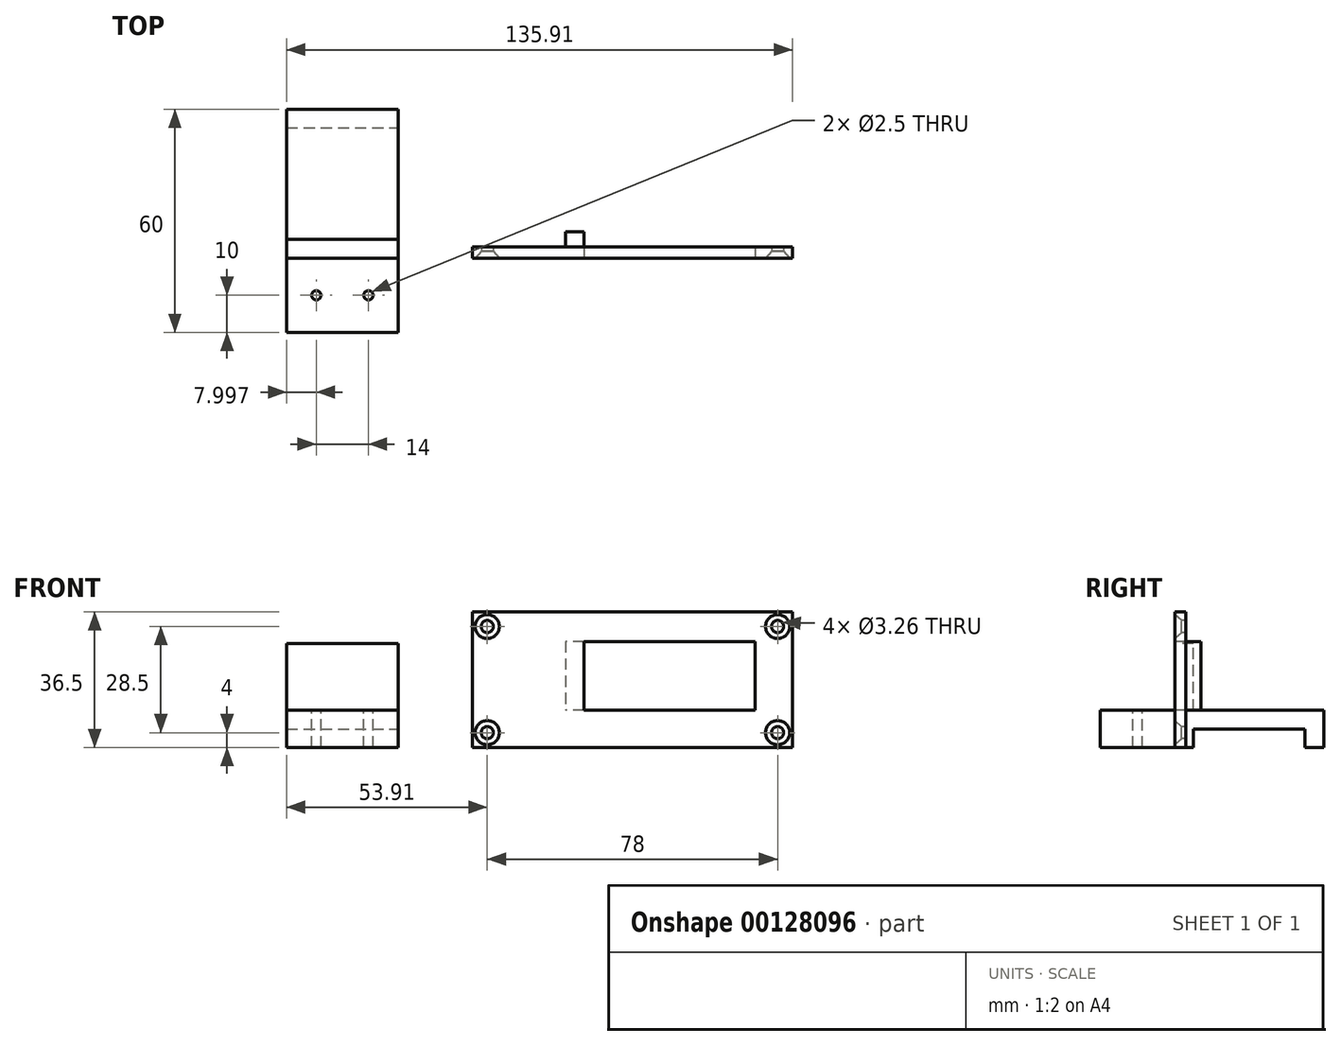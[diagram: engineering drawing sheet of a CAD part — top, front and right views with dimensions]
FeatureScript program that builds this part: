
annotation { "Feature Type Name" : "Feature", "Feature Type Description" : "" }
export const myFeature = defineFeature(function(context is Context, id is Id, definition is map)
    precondition{}
    {
        {
            var Q0;
            Q0=qCreatedBy(makeId("Front.planeOp"),FACE);
            var sketch = newSketch(context, id + "F0", { "sketchPlane" : qUnion([Q0])});
            skLineSegment(sketch, "E0.bottom", {"start": v(0, 18.5) * mm, "end": v(46, 18.5) * mm});
            skLineSegment(sketch, "E0.top", {"start": v(0, 0) * mm, "end": v(46, 0) * mm});
            skLineSegment(sketch, "E0.left", {"start": v(0, 18.5) * mm, "end": v(0, 0) * mm});
            skLineSegment(sketch, "E0.right", {"start": v(46, 18.5) * mm, "end": v(46, 0) * mm});
            skPoint(sketch, "E1.positionSnap0", {"position": v(0, 9.25) * mm});
            skLineSegment(sketch, "E2.bottom", {"start": v(-30, 26.5) * mm, "end": v(56, 26.5) * mm});
            skLineSegment(sketch, "E2.top", {"start": v(-30, -10) * mm, "end": v(56, -10) * mm});
            skLineSegment(sketch, "E2.left", {"start": v(-30, 26.5) * mm, "end": v(-30, -10) * mm});
            skLineSegment(sketch, "E2.right", {"start": v(56, 26.5) * mm, "end": v(56, -10) * mm});
            skPoint(sketch, "E3", {"position": v(52, 22.5) * mm});
            skPoint(sketch, "E4", {"position": v(-26, -6) * mm});
            skPoint(sketch, "E5", {"position": v(-26, 22.5) * mm});
            skPoint(sketch, "E6", {"position": v(52, -6) * mm});
            skLineSegment(sketch, "E7.bottom", {"start": v(0, 18.5) * mm, "end": v(-5, 18.5) * mm});
            skLineSegment(sketch, "E7.top", {"start": v(0, 0) * mm, "end": v(-5, 0) * mm});
            skLineSegment(sketch, "E7.right", {"start": v(-5, 18.5) * mm, "end": v(-5, 0) * mm});
            skSolve(sketch);
        }
        {
            var Q0;
            Q0=makeQuery(id+"F0.imprint","IMPRINT",FACE,{"disambiguationData":[TD([[makeQuery(id+"F0.imprint","IMPRINT",EDGE,{"derivedFrom":sQuery(id+"F0.wireOp",EDGE,"E0.bottom")}),1.0]])]});
            var Q1;
            {var subQ0=sQuery(id+"F0.wireOp",EDGE,"UrZkf7E1-elGO-6lRV-unpn-XGr7alpAxiHO");Q1=makeQuery(id+"F0.imprint","IMPRINT",FACE,{"disambiguationData":[TD([[makeQuery(id+"F0.imprint","IMPRINT",EDGE,{"derivedFrom":subQ0}),1.0]])]});}
            var Q2;
            Q2=makeQuery(id+"F0.imprint","IMPRINT",FACE,{"disambiguationData":[TD([[makeQuery(id+"F0.imprint","IMPRINT",EDGE,{"derivedFrom":sQuery(id+"F0.wireOp",EDGE,"E7.bottom")}),1.0]])]});
            extrude(context, id + "F1", {"entities" : qUnion([Q0, Q1, Q2]), "oppositeDirection" : true, "depth" : 3 * mm});
        }
        {
            var Q0;
            Q0=sQuery(id+"F0.wireOp",VERTEX,"E5");
            var Q1;
            Q1=sQuery(id+"F0.wireOp",VERTEX,"E3");
            var Q2;
            Q2=sQuery(id+"F0.wireOp",VERTEX,"E6");
            var Q3;
            Q3=sQuery(id+"F0.wireOp",VERTEX,"E4");
            var Q4;
            Q4=makeQuery(id+"F1.opExtrude","SWEPT_BODY",BODY,{"disambiguationData":[OSD([sQuery(id+"F0.wireOp",EDGE,"E0.bottom"),sQuery(id+"F0.wireOp",EDGE,"E0.top"),sQuery(id+"F0.wireOp",EDGE,"E0.left"),sQuery(id+"F0.wireOp",EDGE,"E0.right"),sQuery(id+"F0.wireOp",EDGE,"E2.bottom"),sQuery(id+"F0.wireOp",EDGE,"E2.top"),sQuery(id+"F0.wireOp",EDGE,"E2.left"),sQuery(id+"F0.wireOp",EDGE,"E2.right"),sQuery(id+"F0.wireOp",EDGE,"qBcNV5FQ-zFUv-ZIrg-zJPg-vCAjNU29jemr"),sQuery(id+"F0.wireOp",EDGE,"7GAFIpT4-1Big-cPm9-clqv-j1Ld1sRepTig"),sQuery(id+"F0.wireOp",EDGE,"qAZhv7DK-Hoew-V6AH-mbc9-Ry7ODFoE4goo"),sQuery(id+"F0.wireOp",EDGE,"211178a0-aec6-45a9-930c-0d41ed68b8bc.trimOffspring")])]});
            hole(context, id + "F2", {"style" : HoleStyle.C_SINK, "endStyle" : HoleEndStyle.THROUGH, "standardTappedOrClearance" : lookupTablePath({ "standard" : "ANSI", "fit" : "Normal (ASME)", "size" : "#4", "type" : "Clearance" }), "standardBlindInLast" : lookupTablePath({ "fit" : "Free", "standard" : "ANSI", "size" : "#4", "type" : "Clearance" }), "holeDiameter" : 3.26 * mm, "cSinkDiameter" : 6.48 * mm, "cSinkAngle" : 82 * degree, "locations" : qUnion([Q0, Q1, Q2, Q3]), "scope" : qUnion([Q4]), "isTappedThrough" : true});
        }
        {
            var Q0;
            Q0=qCreatedBy(makeId("Front.planeOp"),FACE);
            var sketch = newSketch(context, id + "F3", { "sketchPlane" : qUnion([Q0])});
            skLineSegment(sketch, "E8.bottom", {"start": v(-49.91, 0) * mm, "end": v(-79.91, 0) * mm});
            skLineSegment(sketch, "E8.top", {"start": v(-49.91, -10) * mm, "end": v(-79.91, -10) * mm});
            skLineSegment(sketch, "E8.left", {"start": v(-49.91, 0) * mm, "end": v(-49.91, -10) * mm});
            skLineSegment(sketch, "E8.right", {"start": v(-79.91, 0) * mm, "end": v(-79.91, -10) * mm});
            skLineSegment(sketch, "E9", {"start": v(-79.91, 0) * mm, "end": v(-79.91, 18) * mm});
            skLineSegment(sketch, "E10", {"start": v(-79.91, 18) * mm, "end": v(-49.91, 18) * mm});
            skLineSegment(sketch, "E11", {"start": v(-49.91, 18) * mm, "end": v(-49.91, 0) * mm});
            skPoint(sketch, "E12.endSnap0", {"position": v(-49.91, -5) * mm});
            skSolve(sketch);
        }
        {
            var Q0;
            Q0=makeQuery(id+"F3.imprint","IMPRINT",FACE,{"disambiguationData":[TD([[makeQuery(id+"F3.imprint","IMPRINT",EDGE,{"derivedFrom":sQuery(id+"F3.wireOp",EDGE,"E8.bottom")}),-1.0]])]});
            var Q1;
            Q1=makeQuery(id+"F3.imprint","IMPRINT",FACE,{"disambiguationData":[TD([[makeQuery(id+"F3.imprint","IMPRINT",EDGE,{"derivedFrom":sQuery(id+"F3.wireOp",EDGE,"E8.bottom")}),1.0]])]});
            extrude(context, id + "F4", {"entities" : qUnion([Q0, Q1]), "oppositeDirection" : true, "depth" : 5 * mm});
        }
        {
            var Q0;
            Q0=makeQuery(id+"F3.imprint","IMPRINT",FACE,{"disambiguationData":[TD([[makeQuery(id+"F3.imprint","IMPRINT",EDGE,{"derivedFrom":sQuery(id+"F3.wireOp",EDGE,"E8.bottom")}),1.0]])]});
            extrude(context, id + "F5", {"entities" : qUnion([Q0]), "operationType" : NewBodyOperationType.ADD, "oppositeDirection" : true, "depth" : 40 * mm, "hasSecondDirection" : true, "secondDirectionOppositeDirection" : false, "secondDirectionDepth" : 20 * mm});
        }
        {
            var Q0;
            {var subQ0=sQuery(id+"F3.wireOp",EDGE,"E8.top");Q0=makeQuery(id+"F5.boolean.opBoolean","MERGE",FACE,{"derivedFrom":[makeQuery(id+"F4.opExtrude","SWEPT_FACE",FACE,{"disambiguationData":[OSD([subQ0])]}),makeQuery(id+"F5.opExtrude","SWEPT_FACE",FACE,{"disambiguationData":[OSD([subQ0])]})]});}
            var sketch = newSketch(context, id + "F6", { "sketchPlane" : qUnion([Q0])});
            skLineSegment(sketch, "E13.bottom", {"start": v(-79.91, -35) * mm, "end": v(-49.91, -35) * mm});
            skLineSegment(sketch, "E13.top", {"start": v(-79.91, -5) * mm, "end": v(-49.91, -5) * mm});
            skLineSegment(sketch, "E13.left", {"start": v(-79.91, -35) * mm, "end": v(-79.91, -5) * mm});
            skLineSegment(sketch, "E13.right", {"start": v(-49.91, -35) * mm, "end": v(-49.91, -5) * mm});
            skSolve(sketch);
        }
        {
            var Q0;
            Q0=makeQuery(id+"F6.imprint","IMPRINT",FACE,{"disambiguationData":[TD([[makeQuery(id+"F6.imprint","IMPRINT",EDGE,{"derivedFrom":sQuery(id+"F6.wireOp",EDGE,"E13.bottom")}),1.0]])]});
            extrude(context, id + "F7", {"entities" : qUnion([Q0]), "operationType" : NewBodyOperationType.REMOVE, "oppositeDirection" : true, "depth" : 5 * mm});
        }
        {
            var Q0;
            {var subQ1=sQuery(id+"F3.wireOp",EDGE,"E8.left");var subQ2=sQuery(id+"F3.wireOp",EDGE,"E8.right");var subQ3=sQuery(id+"F3.wireOp",EDGE,"E8.top");var subQ4=sQuery(id+"F3.wireOp",EDGE,"E8.bottom");Q0=makeQuery(id+"F5.boolean.opBoolean","SPLIT",FACE,{"disambiguationData":[TD([makeQuery(id+"F5.opExtrude","CAP_FACE",FACE,{"disambiguationData":[OSD([subQ4,subQ3,subQ1,subQ2])],"isStart":true})])],"derivedFrom":makeQuery(id+"F5.opExtrude","SWEPT_FACE",FACE,{"disambiguationData":[OSD([subQ4])]})});}
            var sketch = newSketch(context, id + "F8", { "sketchPlane" : qUnion([Q0])});
            skPoint(sketch, "E14", {"position": v(-57.91, -10) * mm});
            skPoint(sketch, "E14.positionSnap0", {"position": v(-49.91, -10) * mm});
            skPoint(sketch, "E15", {"position": v(-71.91, -10) * mm});
            skPoint(sketch, "E15.positionSnap0", {"position": v(-79.91, -10) * mm});
            skSolve(sketch);
        }
        {
            var Q0;
            Q0=sQuery(id+"F8.wireOp",VERTEX,"E15");
            var Q1;
            Q1=sQuery(id+"F8.wireOp",VERTEX,"E14");
            var Q2;
            Q2=makeQuery(id+"F4.opExtrude","SWEPT_BODY",BODY,{"disambiguationData":[OSD([sQuery(id+"F3.wireOp",EDGE,"E8.top"),sQuery(id+"F3.wireOp",EDGE,"E8.left"),sQuery(id+"F3.wireOp",EDGE,"E8.right"),sQuery(id+"F3.wireOp",EDGE,"E9"),sQuery(id+"F3.wireOp",EDGE,"E10"),sQuery(id+"F3.wireOp",EDGE,"E11")])]});
            hole(context, id + "F9", {"style" : HoleStyle.SIMPLE, "endStyle" : HoleEndStyle.THROUGH, "holeDiameter" : 2.5 * mm, "locations" : qUnion([Q0, Q1]), "scope" : qUnion([Q2]), "isTappedThrough" : true});
        }
        {
            var Q0;
            Q0=makeQuery(id+"F0.imprint","IMPRINT",FACE,{"disambiguationData":[TD([[makeQuery(id+"F0.imprint","IMPRINT",EDGE,{"derivedFrom":sQuery(id+"F0.wireOp",EDGE,"E7.bottom")}),1.0]])]});
            extrude(context, id + "F10", {"entities" : qUnion([Q0]), "operationType" : NewBodyOperationType.ADD, "oppositeDirection" : true, "depth" : 7 * mm});
        }
    });
